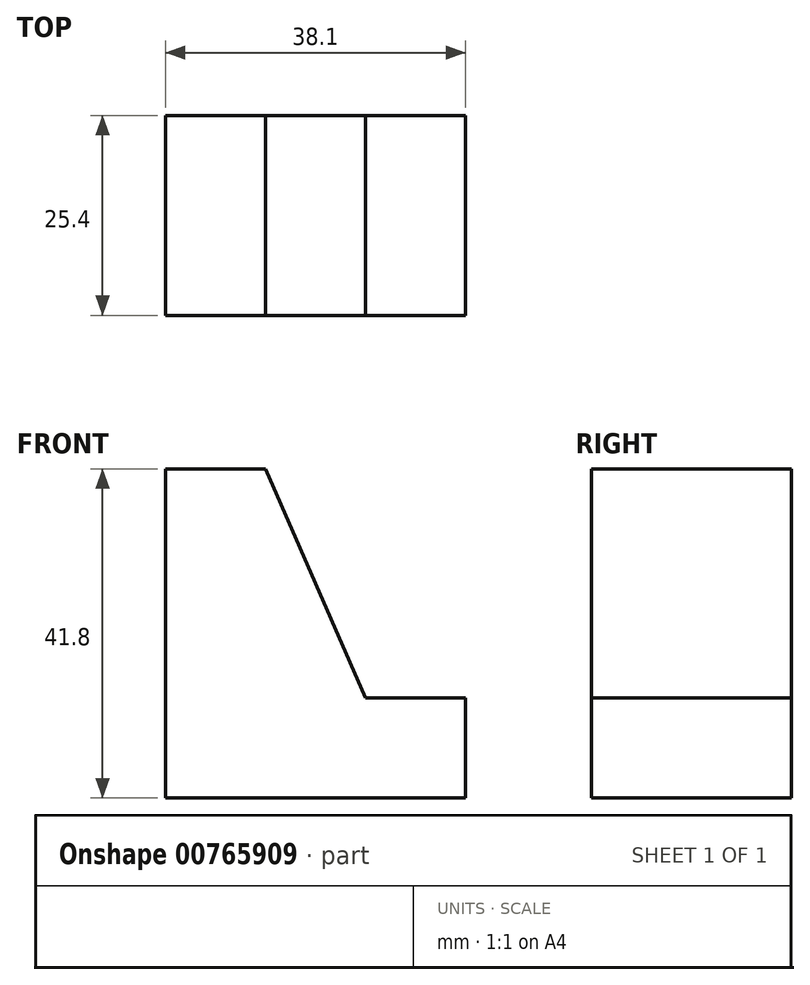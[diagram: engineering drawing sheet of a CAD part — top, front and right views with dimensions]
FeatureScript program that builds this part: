
annotation { "Feature Type Name" : "Feature", "Feature Type Description" : "" }
export const myFeature = defineFeature(function(context is Context, id is Id, definition is map)
    precondition{}
    {
        {
            var Q0;
            Q0=qCreatedBy(makeId("Front.planeOp"),FACE);
            var sketch = newSketch(context, id + "F0", { "sketchPlane" : qUnion([Q0])});
            skLineSegment(sketch, "E0", {"start": v(0, 0) * mm, "end": v(38.1, 0) * mm});
            skLineSegment(sketch, "E1", {"start": v(38.1, 0) * mm, "end": v(38.1, 12.7) * mm});
            skLineSegment(sketch, "E2", {"start": v(38.1, 12.7) * mm, "end": v(25.4, 12.7) * mm});
            skLineSegment(sketch, "E3", {"start": v(25.4, 12.7) * mm, "end": v(12.7, 41.8) * mm});
            skLineSegment(sketch, "E4", {"start": v(12.7, 41.8) * mm, "end": v(0, 41.8) * mm});
            skLineSegment(sketch, "E5", {"start": v(0, 41.8) * mm, "end": v(0, 0) * mm});
            skSolve(sketch);
        }
        {
            var Q0;
            Q0 = qSketchRegion(id + "F0", true);
            extrude(context, id + "F1", {"entities" : qUnion([Q0]), "depth" : 25.4 * mm, "offsetDistance" : 25.4 * mm});
        }
    });
